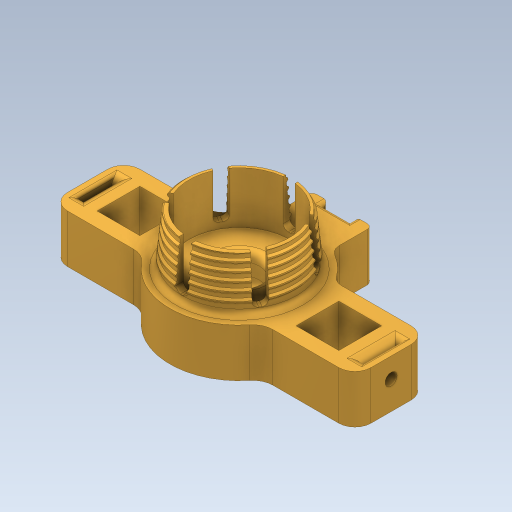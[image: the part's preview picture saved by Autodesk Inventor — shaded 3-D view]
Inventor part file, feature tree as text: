
AUTODESK INVENTOR PART (.ipt)
format: ipt  version: 2023 (Build 270158000, 158)  size: 3,056,640 bytes
history: native  units: mm
features: fillet x11, sketch x7, extrude x5, hole x3, helix x2, direct_edit x2, draft x1, plane x1, mirror x1, other x1, revolve x1
ambient origin geometry x8: Origin, YZ Plane, XZ Plane, XY Plane, X Axis, Y Axis, Z Axis, Center Point
bodies: Solid1 (feature_tree)
feature tree (35):
  extrude  "Extrusion1"  Depth=26.5mm
  draft  "FaceDraft1"
  sketch  "Sketch2"  dims[d34=0.0mm d35=0.0mm d56=8.726646mm]
  helix  "Coil3"  [1 undecoded]
  helix  "Coil4"  [1 undecoded]
  direct_edit  "Direct Edit2"
  extrude  "Extrusion2"  Depth=8.726646mm
  extrude  "Extrusion13"  TaperAngle=90.0deg  [1 undecoded]
  plane  "Work Plane5"
  extrude  "Extrusion14"  Depth=34.58632mm
  hole  "Hole3"  [1 undecoded]
  hole  "Hole4"  [1 undecoded]
  fillet  "Fillet11"  Radius=60.0mm
  fillet  "Fillet22"  [1 undecoded]
  hole  "Hole6"  [1 undecoded]
  mirror  "Mirror3"
  extrude  "Extrusion15"  Depth=1.2mm
  direct_edit  "Direct Edit3"
  fillet  "Fillet23"  Radius=18.0mm
  fillet  "Fillet13"  Radius=10.65mm
  fillet  "Fillet15"  Radius=10.0mm
  fillet  "Fillet16"  Radius=15.0mm
  fillet  "Fillet17"  Radius=10.0mm
  fillet  "Fillet18"  Radius=7.0mm
  fillet  "Fillet19"  Radius=10.0mm
  fillet  "Fillet20"  Radius=1.0mm
  fillet  "Fillet21"  [1 undecoded]
  sketch  "Sketch1"  dims[d0=25.0mm d1=26.5mm d2=12.875mm d3=0.0mm d4=1.047198mm]
  sketch  "Sketch3"  dims[d62=2.0mm d63=10.15mm d64=10.0mm d65=1.047198mm]
  sketch  "Sketch13"  dims[d66=90.0deg d67=90.0deg d68=0.0mm d69=0.0mm d70=2.0mm d71=3.0mm d72=10.0mm d73=-1.047198mm d74=90.0deg d75=90.0deg d76=0.0mm d77=0.0mm]
  sketch  "Sketch14"  dims[d79=-0.127mm d145=34.58632mm]
  sketch  "Sketch16"  dims[d150=120.0deg d151=120.0deg]
  sketch  "Sketch17"  dims[d153=21.6866mm d157=12.0mm d158=0.0mm d160=60.0mm d162=360.0deg d164=0.0mm d165=0.0mm d179=5.3mm d180=6.0mm d181=4.0mm d182=2.0mm d183=90.0deg d184=5.0mm d185=0.0mm d186=10.0mm d187=6.0mm d188=4.0mm d189=2.0mm d190=90.0deg d191=7.0mm d192=0.0mm d193=2.0mm d194=20.0mm d195=18.0mm d196=10.65mm d197=10.0mm d206=15.0mm d207=10.0mm d208=7.0mm d209=10.0mm d210=1.0mm d211=0.0mm d212=-4.363323mm d213=1.0mm d215=1.5mm d216=3.0mm d217=8.0mm d219=1.0mm d220=5.0mm d221=3.0mm d222=6.0mm d223=4.0mm d224=2.0mm d225=90.0deg d226=6.5mm d227=0.0mm d228=3.0mm d229=5.0mm d230=4.0mm d234=2.0mm d235=0.7mm d237=1.5mm d238=1.2mm d239=1.3mm d240=1.2mm d109=0.5mm d110=0.872665mm d111=0.5mm d112=0.872665mm d236=0.5mm]
  other  "Size2"
  revolve  "Rotate1"  [1 undecoded]
note: 9 required parameter values undecoded (feature->parameter linkage not recoverable at this tier; creation-order binding heuristic only, values carry confidence <= 0.55)